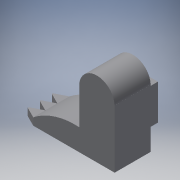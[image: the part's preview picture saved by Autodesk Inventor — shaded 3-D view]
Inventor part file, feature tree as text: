
AUTODESK INVENTOR PART (.ipt)
format: ipt  version: 2016 (Build 200138000, 138)  size: 212,992 bytes
history: native  units: in
note: dims shown in document units (in); Inventor stores cm internally (conversion verified against a paired STEP export)
features: extrude x10, sketch x10, reference x9, plane x1, fillet x1
ambient origin geometry x8: Origin, YZ Plane, XZ Plane, XY Plane, X Axis, Y Axis, Z Axis, Center Point
bodies: Solid1 (feature_tree)
feature tree (31):
  extrude  "Extrusion1"  Depth=0.0098in
  extrude  "Extrusion2"  Depth=0.0098in
  extrude  "Extrusion3"  Depth=0.1969in
  extrude  "Extrusion5"  Depth=0.6in
  extrude  "Extrusion6"  Depth=1.0in TaperAngle=0.0deg
  plane  "Work Plane1"
  extrude  "Extrusion7"  Depth=0.2in TaperAngle=0.0deg
  extrude  "Extrusion8"  [1 undecoded]
  extrude  "Extrusion9"  Depth=0.0394in
  extrude  "Extrusion10"  Depth=0.2362in TaperAngle=0.0deg
  fillet  "Fillet1"  Radius=0.5in
  extrude  "Extrusion11"  Depth=0.1969in
  sketch  "Sketch1"  dims[d0=0.0098in d1=0.0098in]
  reference  "Reference1"
  reference  "Reference2"
  reference  "Reference3"
  reference  "Reference4"
  reference  "Reference5"
  sketch  "Sketch2"  dims[d2=0.0098in d3=0.0098in]
  sketch  "Sketch3"  dims[d4=0.1969in d5=0.0in d6=0.98in]
  reference  "Reference6"
  sketch  "Sketch5"  dims[d7=1.0in d8=0.0in d9=0.6in]
  sketch  "Sketch6"  dims[d10=2.25in d12=1.0in d13=0.0in]
  sketch  "Sketch7"  dims[d16=0.3333in d22=0.2in d23=0.0in]
  reference  "Reference7"
  sketch  "Sketch8"  dims[d24=100.0in d25=0.0in d26=-0.5in]
  reference  "Reference8"
  sketch  "Sketch9"  dims[d27=0.0394in d28=0.0394in]
  sketch  "Sketch10"  dims[d29=0.0394in d30=0.2362in d31=0.0in d32=0.5in d33=0.0in]
  reference  "Reference9"
  sketch  "Sketch11"  dims[d34=0.1378in d35=0.1969in d36=0.1969in d37=0.1211in d38=0.1211in d39=0.1969in d40=0.0in d41=0.1969in d42=0.0in d43=0.0197in d44=0.5in d45=0.2in d46=0.0in]
note: 1 required parameter value undecoded (feature->parameter linkage not recoverable at this tier; creation-order binding heuristic only, values carry confidence <= 0.55)
